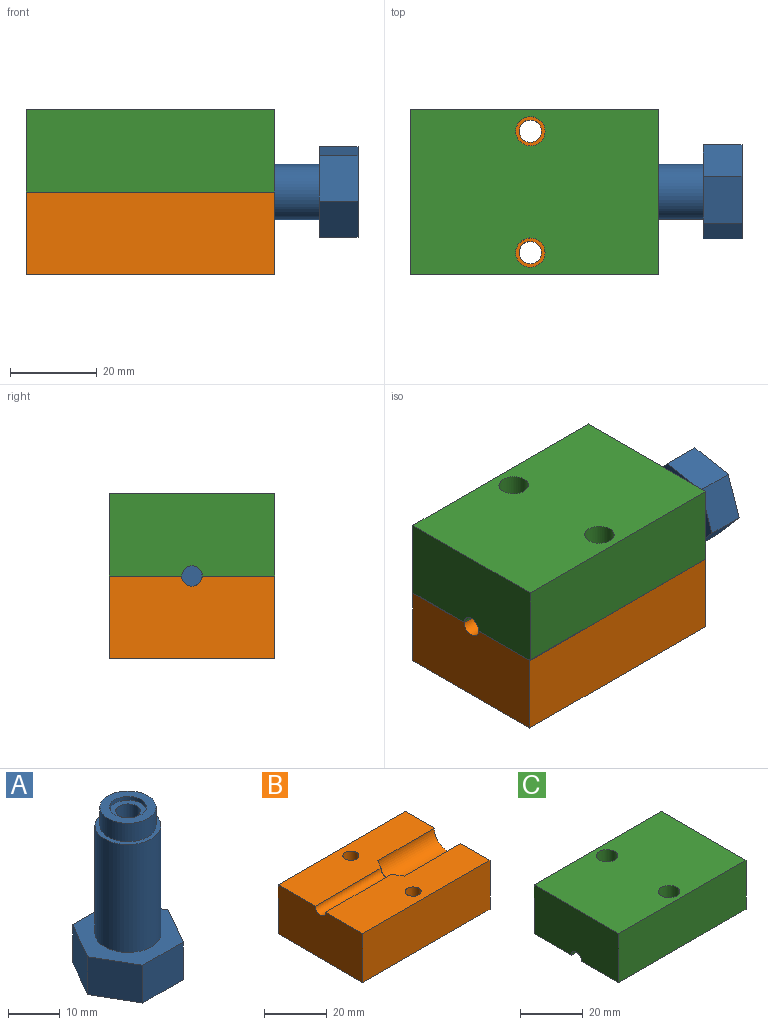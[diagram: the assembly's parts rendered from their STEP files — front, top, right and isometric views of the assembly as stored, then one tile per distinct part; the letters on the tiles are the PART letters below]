
ASSEMBLY  parts=3 mates=2
PART A: 16 faces, bbox 22x19.1x38.6 mm
  f0: plane 9.53x8.89mm, normal (-0.87,0.5,0), area 97.8mm2, adj f1,f5,f6,f7
  f1: plane 9.53x8.89mm, normal (-0.87,-0.5,0), area 97.8mm2, adj f0,f2,f6,f7
  f2: plane 11x8.89mm, normal (0,-1,0), area 97.8mm2, adj f1,f3,f6,f7
  f3: plane 9.53x8.89mm, normal (0.87,-0.5,0), area 97.8mm2, adj f2,f4,f6,f7
  f4: plane 9.53x8.89mm, normal (0.87,0.5,0), area 97.8mm2, adj f3,f5,f6,f7
  f5: plane 11x8.89mm, normal (0,1,0), area 97.8mm2, adj f0,f4,f6,f7
  f6: plane 22x19.05mm, normal (0,0,1), area 187.6mm2, adj f0,f1,f2,f3,f4,f5,f8
  f7: plane 22x19.05mm, normal (0,0,-1), area 314.3mm2, adj f0,f1,f2,f3,f4,f5
  f8: cylinder r=6.35mm len=25.4mm, axis (0,0,-1), area 1013.4mm2, adj f6,f9
  f9: plane 12.7x12.7mm, normal (0,0,1), area 35.2mm2, adj f8,f10
  f10: cylinder r=5.4mm len=10.8mm, axis (0,0,-1), area 146.4mm2, adj f9,f11
  f11: plane 10.8x10.8mm, normal (0,0,1), area 51.8mm2, adj f10,f12
  f12: cylinder r=3.56mm len=7.11mm, axis (0,0,1), area 19.9mm2, adj f11,f13
  f13: plane 7.11x7.11mm, normal (0,0,1), area 22.4mm2, adj f12,f14
  f14: cylinder r=2.35mm len=8.84mm, axis (0,0,1), area 130.5mm2, adj f13,f15
  f15: plane 4.7x4.7mm, normal (0,0,1), area 17.3mm2, adj f14
PART B: 12 faces, bbox 57.2x38.1x19.1 mm
  f0: plane 57.15x16.7mm, normal (0,0,1), area 838.5mm2, adj f2,f3,f5,f6,f8,f9,f10
  f1: plane 57.15x16.7mm, normal (0,0,1), area 838.5mm2, adj f2,f3,f4,f5,f8,f9,f11
  f2: plane 38.1x19.05mm, normal (-1,0,0), area 717.1mm2, adj f0,f1,f4,f6,f7,f9
  f3: cone r=0mm half-angle=59deg, axis (1,0,0), area 54.8mm2, adj f0,f1,f8,f9
  f4: plane 57.15x19.05mm, normal (0,-1,0), area 1088.7mm2, adj f1,f2,f5,f7
  f5: plane 38.1x19.05mm, normal (1,0,0), area 670.1mm2, adj f0,f1,f4,f6,f7,f8
  f6: plane 57.15x19.05mm, normal (0,1,0), area 1088.7mm2, adj f0,f2,f5,f7
  f7: plane 57.15x38.1mm, normal (0,0,-1), area 2136.5mm2, adj f2,f4,f5,f6,f10,f11
  f8: cylinder r=5.95mm len=25.4mm, axis (1,0,0), area 475.1mm2, adj f0,f1,f3,f5
  f9: cylinder r=2.35mm len=29.58mm, axis (-1,0,0), area 218.4mm2, adj f0,f1,f2,f3
  f10: cylinder r=2.55mm len=19.05mm, axis (0,0,1), area 305.5mm2, adj f0,f7
  f11: cylinder r=2.55mm len=19.05mm, axis (0,0,1), area 305.5mm2, adj f1,f7
PART C: 12 faces, bbox 57.2x38.1x19.1 mm
  f0: plane 57.15x16.7mm, normal (0,0,-1), area 823.1mm2, adj f2,f3,f5,f6,f8,f9,f11
  f1: plane 57.15x16.7mm, normal (0,0,-1), area 823.1mm2, adj f2,f3,f4,f6,f8,f9,f10
  f2: cone r=0mm half-angle=59deg, axis (1,0,0), area 54.8mm2, adj f0,f1,f8,f9
  f3: plane 38.1x19.05mm, normal (1,0,0), area 670.1mm2, adj f0,f1,f4,f5,f7,f8
  f4: plane 57.15x19.05mm, normal (0,-1,0), area 1088.7mm2, adj f1,f3,f6,f7
  f5: plane 57.15x19.05mm, normal (0,1,0), area 1088.7mm2, adj f0,f3,f6,f7
  f6: plane 38.1x19.05mm, normal (-1,0,0), area 717.1mm2, adj f0,f1,f4,f5,f7,f9
  f7: plane 57.15x38.1mm, normal (0,0,1), area 2105.7mm2, adj f3,f4,f5,f6,f10,f11
  f8: cylinder r=5.95mm len=25.4mm, axis (1,0,0), area 475.1mm2, adj f0,f1,f2,f3
  f9: cylinder r=2.35mm len=29.58mm, axis (-1,0,0), area 218.4mm2, adj f0,f1,f2,f6
  f10: cylinder r=3.38mm len=19.05mm, axis (0,0,1), area 404.4mm2, adj f1,f7
  f11: cylinder r=3.38mm len=19.05mm, axis (0,0,1), area 404.4mm2, adj f0,f7
PLACE A rot(axis=(-0.68,-0.25,0.68),151.4deg) t=(45.88,7.02,12.22)mm
PLACE B t=(-1.96,7.02,12.22)mm fixed
PLACE C t=(-1.94,6.97,12.22)mm
MATE fastened B.f1 <-> C.f1  axis (0,0,1) through (-3.68,-4.35,12.22)mm
MATE cylindrical A.f8 <-> B.f3  axis (-1,0,0) through (7.27,7.02,12.22)mm
